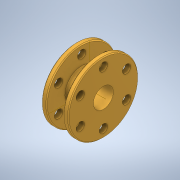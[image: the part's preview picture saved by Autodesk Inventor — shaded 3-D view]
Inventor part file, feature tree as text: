
AUTODESK INVENTOR PART (.ipt)
format: ipt  version: 2021.1 (Build 251245000, 245)  size: 196,096 bytes
history: native  units: in
note: dims shown in document units (in); Inventor stores cm internally (conversion verified against a paired STEP export)
features: chamfer x3, sketch x3, projected_geometry x3, extrude x2, revolve x1
ambient origin geometry x8: Origin, YZ Plane, XZ Plane, XY Plane, X Axis, Y Axis, Z Axis, Center Point
bodies: Solid1 (feature_tree)
feature tree (12):
  extrude  "Extrusion1"  Depth=2.0in
  revolve  "Revolution1"  [1 undecoded]
  chamfer  "Chamfer1"  Distance=1.1in
  chamfer  "Chamfer2"  Distance=0.3in
  chamfer  "Chamfer3"  Angle=90.0deg  [1 undecoded]
  extrude  "Extrusion2"  Depth=0.3in TaperAngle=45.0deg
  sketch  "Sketch1"  dims[d0=1.2in d1=2.0in]
  sketch  "Sketch2"  dims[d2=1.6in d3=0.0in d4=1.1in]
  projected_geometry  "Projected Loop1"
  sketch  "Sketch3"  dims[d5=0.3in d6=1.1in d7=0.3in d8=90.0deg d9=0.05in d10=0.125in d11=45.0deg d12=0.05in d13=0.125in d14=45.0deg d15=0.05in d16=0.125in d17=45.0deg d18=3.2in d19=0.5in d20=2.3622in d22=360.0deg d24=0.0in d25=0.0in]
  projected_geometry  "Project Cut Edges1"
  projected_geometry  "Project Cut Edges2"
note: 2 required parameter values undecoded (feature->parameter linkage not recoverable at this tier; creation-order binding heuristic only, values carry confidence <= 0.55)